# Revit family: KEUCO_53987010000
name_source: partatom
category: Sonderausstattung
revit_build: Autodesk Revit 2016 (Build: 20150220_1215(x64)
units: mm (PartAtom-declared; Revit-internal decimal feet)

## family parameters
Arbeitsebenenbasiert = Nein
Beim Laden mit Abzugskörper schneiden = Nein
Bemaßung runder Anschluss = Durchmesser verwenden
Gemeinsam genutzt = Nein
Immer vertikal = Ja
OmniClass-Nummer = 23.45.00.00
Raumberechnungspunkt = Nein
Teiletyp = Normal

## types (1)
- 53987010000
    Artikelnummer = 53987010000
    Ausschreibungstext = KEUCO PLAN BLUE Brause-Set, 53987010000, 
verchromt, bestehend aus:
- Wandstange 800 mm (Gesamthöhe 850 mm) mit   
  Brauseschieber, Höhenverstellung mit Griff,
  Neigungswinkel stufenlos einstellbar
- Fliesenausgleichsscheibe (5 mm)
- Handbrause mit Normal-, Soft- und Massagestrahl
- Brauseschlauch, 1600 mm
Die Wandstange wird verdeckt angebracht,
Lieferung inkl. korrosionsfreiem Befestigungsmaterial
    Beschreibung = bestehend aus:
- Wandstange 800 mm mit Brauseschieber,
  Höhenverstellung mit Griff, Neigungswinkel verstellbar
- Fliesenausgleichscheibe (5 mm)
- Handbrause mit Normal-, Soft-, und Massagestrahl
- Brauseschlauch, 1600 mm
    Gewicht = 1.408
    Hersteller = KEUCO
    Kategorie = ARM
    Preisgruppe = 1
    Serie = IXMO
    Stange Länge = 800 mm  [stored 2.62467 ft]
    URL = https://www.keuco.com
    Verwendung = DU / WA

note: [stored X ft] marks values corroborated as IEEE doubles in the binary element streams (Revit-internal decimal feet)

## geometry (parser evidence)
native form markers: Blend x2, Sweep x5
no freeform markers — native parametric forms only
